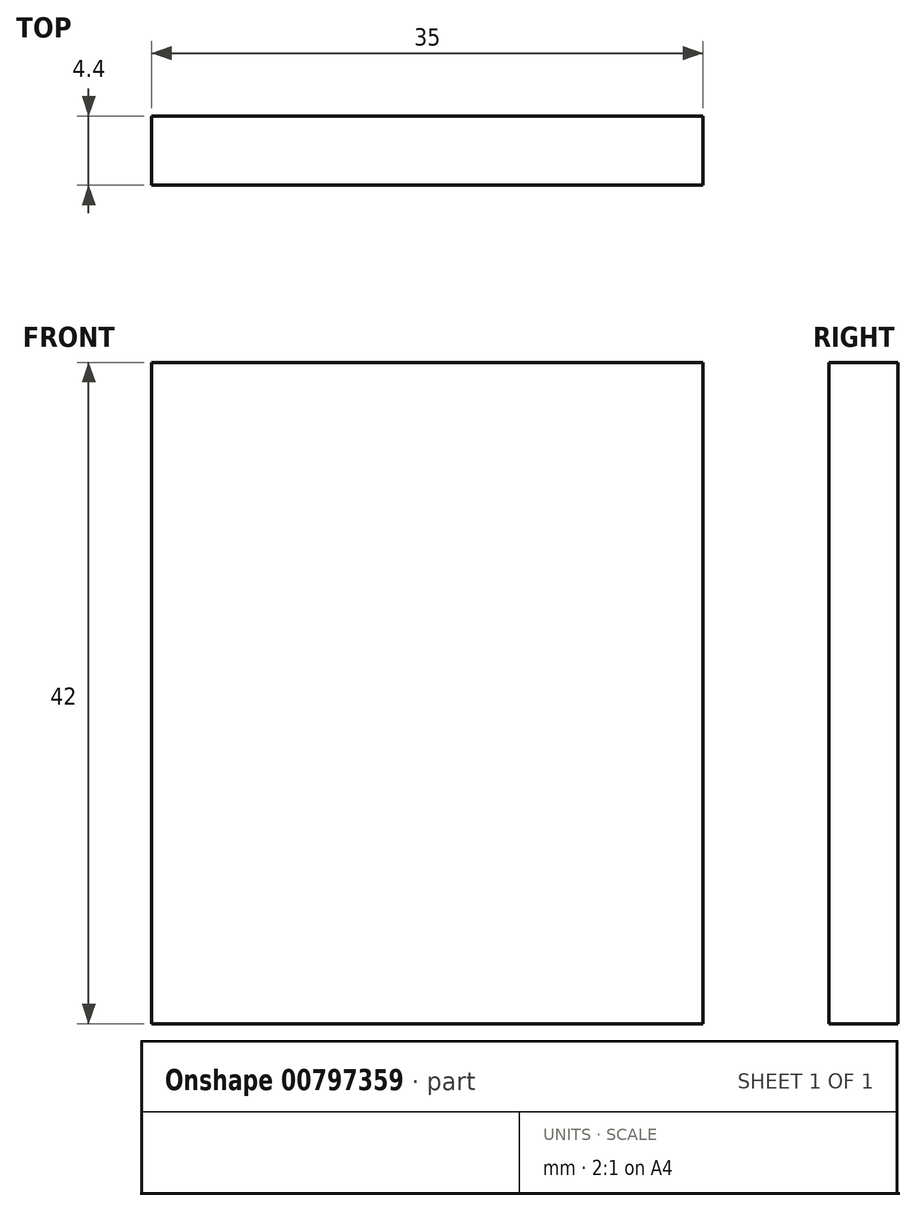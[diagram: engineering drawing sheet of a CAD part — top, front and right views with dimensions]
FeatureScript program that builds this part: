
annotation { "Feature Type Name" : "Feature", "Feature Type Description" : "" }
export const myFeature = defineFeature(function(context is Context, id is Id, definition is map)
    precondition{}
    {
        {
            var Q0;
            Q0=qCreatedBy(makeId("Front.planeOp"),FACE);
            var sketch = newSketch(context, id + "F0", { "sketchPlane" : qUnion([Q0])});
            skLineSegment(sketch, "E0.top", {"start": v(-17.5, 21) * mm, "end": v(17.5, 21) * mm});
            skLineSegment(sketch, "E0.left", {"start": v(-17.5, -21) * mm, "end": v(-17.5, 21) * mm});
            skLineSegment(sketch, "E0.right", {"start": v(17.5, -21) * mm, "end": v(17.5, 21) * mm});
            skLineSegment(sketch, "E1", {"start": v(-17.5, -21) * mm, "end": v(17.5, -21) * mm});
            skLineSegment(sketch, "E2", {"start": v(-17.5, -21) * mm, "end": v(17.5, 21) * mm, "construction": true});
            skSolve(sketch);
        }
        {
            var Q0;
            Q0 = qSketchRegion(id + "F0", true);
            extrude(context, id + "F1", {"entities" : qUnion([Q0]), "depth" : 4.4 * mm, "offsetDistance" : 25 * mm});
        }
    });
